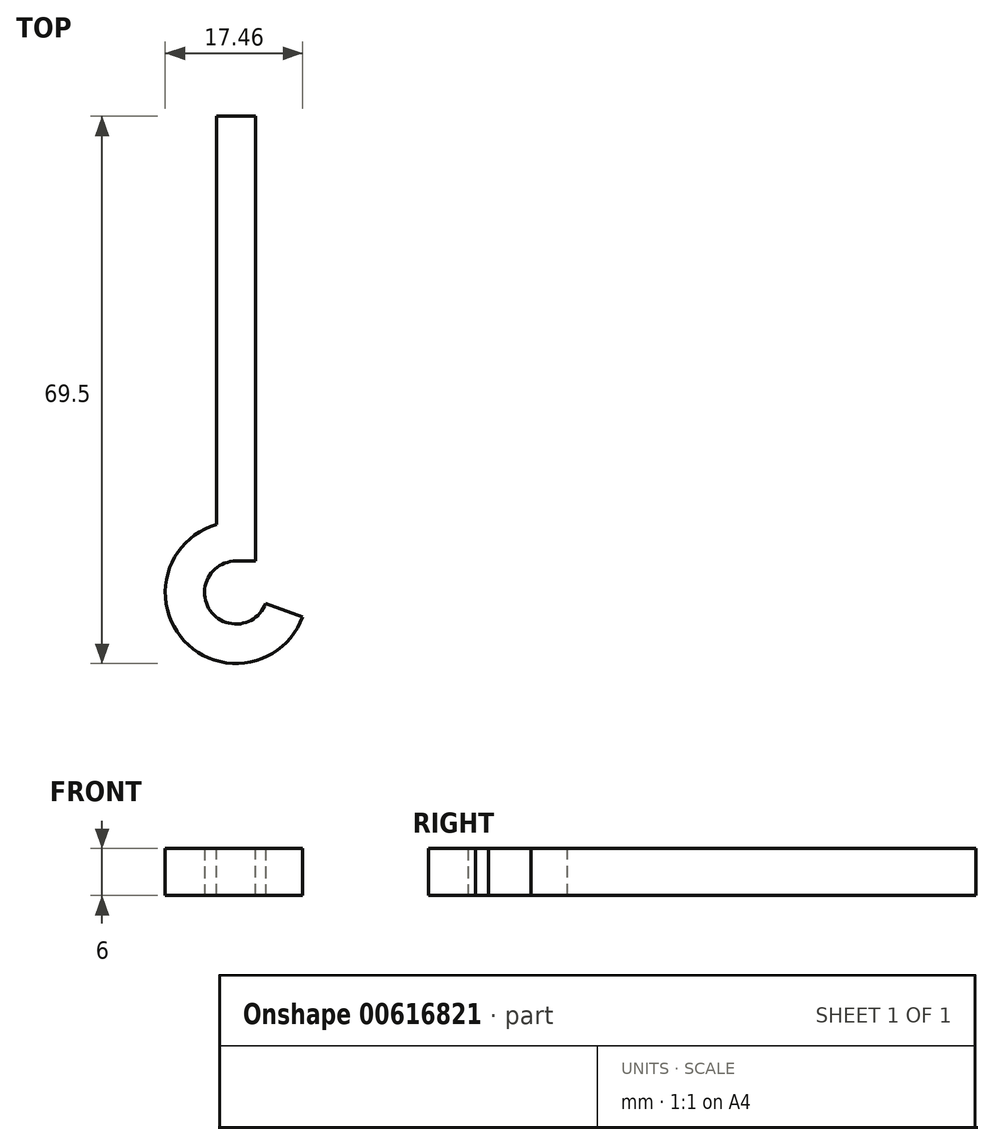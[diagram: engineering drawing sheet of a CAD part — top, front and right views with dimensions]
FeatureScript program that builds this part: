
annotation { "Feature Type Name" : "Feature", "Feature Type Description" : "" }
export const myFeature = defineFeature(function(context is Context, id is Id, definition is map)
    precondition{}
    {
        {
            var Q0;
            Q0=qCreatedBy(makeId("Front.planeOp"),FACE);
            var sketch = newSketch(context, id + "F0", { "sketchPlane" : qUnion([Q0])});
            skLineSegment(sketch, "E0.bottom", {"start": v(2.5, 3) * mm, "end": v(-2.5, 3) * mm});
            skLineSegment(sketch, "E0.top", {"start": v(2.5, -3) * mm, "end": v(-2.5, -3) * mm});
            skLineSegment(sketch, "E0.left", {"start": v(2.5, 3) * mm, "end": v(2.5, -3) * mm});
            skLineSegment(sketch, "E0.right", {"start": v(-2.5, 3) * mm, "end": v(-2.5, -3) * mm});
            skPoint(sketch, "E0.middle", {"position": v(0, 0) * mm});
            skSolve(sketch);
        }
        {
            var Q0;
            Q0=qCreatedBy(makeId("Top.planeOp"),FACE);
            var sketch = newSketch(context, id + "F1", { "sketchPlane" : qUnion([Q0])});
            skLineSegment(sketch, "E1", {"start": v(0, 0) * mm, "end": v(0, -54) * mm});
            skArc(sketch, "E2", {"start": v(0, -54) * mm, "mid": v(-5.32, -64.23) * mm, "end": v(6.1, -62.72) * mm});
            skLineSegment(sketch, "E3", {"start": v(0, -60.5) * mm, "end": v(31.27, -60.5) * mm, "construction": true});
            skLineSegment(sketch, "E4", {"start": v(0, -60.5) * mm, "end": v(6.1, -62.72) * mm, "construction": true});
            skSolve(sketch);
        }
        {
            var Q0;
            Q0=makeQuery(id+"F0.imprint","IMPRINT",FACE,{"disambiguationData":[TD([[makeQuery(id+"F0.imprint","IMPRINT",EDGE,{"derivedFrom":sQuery(id+"F0.wireOp",EDGE,"E0.bottom")}),1.0]])]});
            var Q1;
            Q1=sQuery(id+"F1.wireOp",EDGE,"E1");
            var Q2;
            Q2=sQuery(id+"F1.wireOp",EDGE,"IuiSgRfH-xPEr-80Ew-aSqa-VCSLa5j1DbUe");
            var Q3;
            Q3=sQuery(id+"F1.wireOp",EDGE,"dd1b8111-9d08-458b-843d-f6c00407ebb7.filletArc");
            var Q4;
            Q4=sQuery(id+"F1.wireOp",EDGE,"E2");
            sweep(context, id + "F2", {"profiles" : qUnion([Q0]), "path" : qUnion([Q1, Q2, Q3, Q4])});
        }
    });
